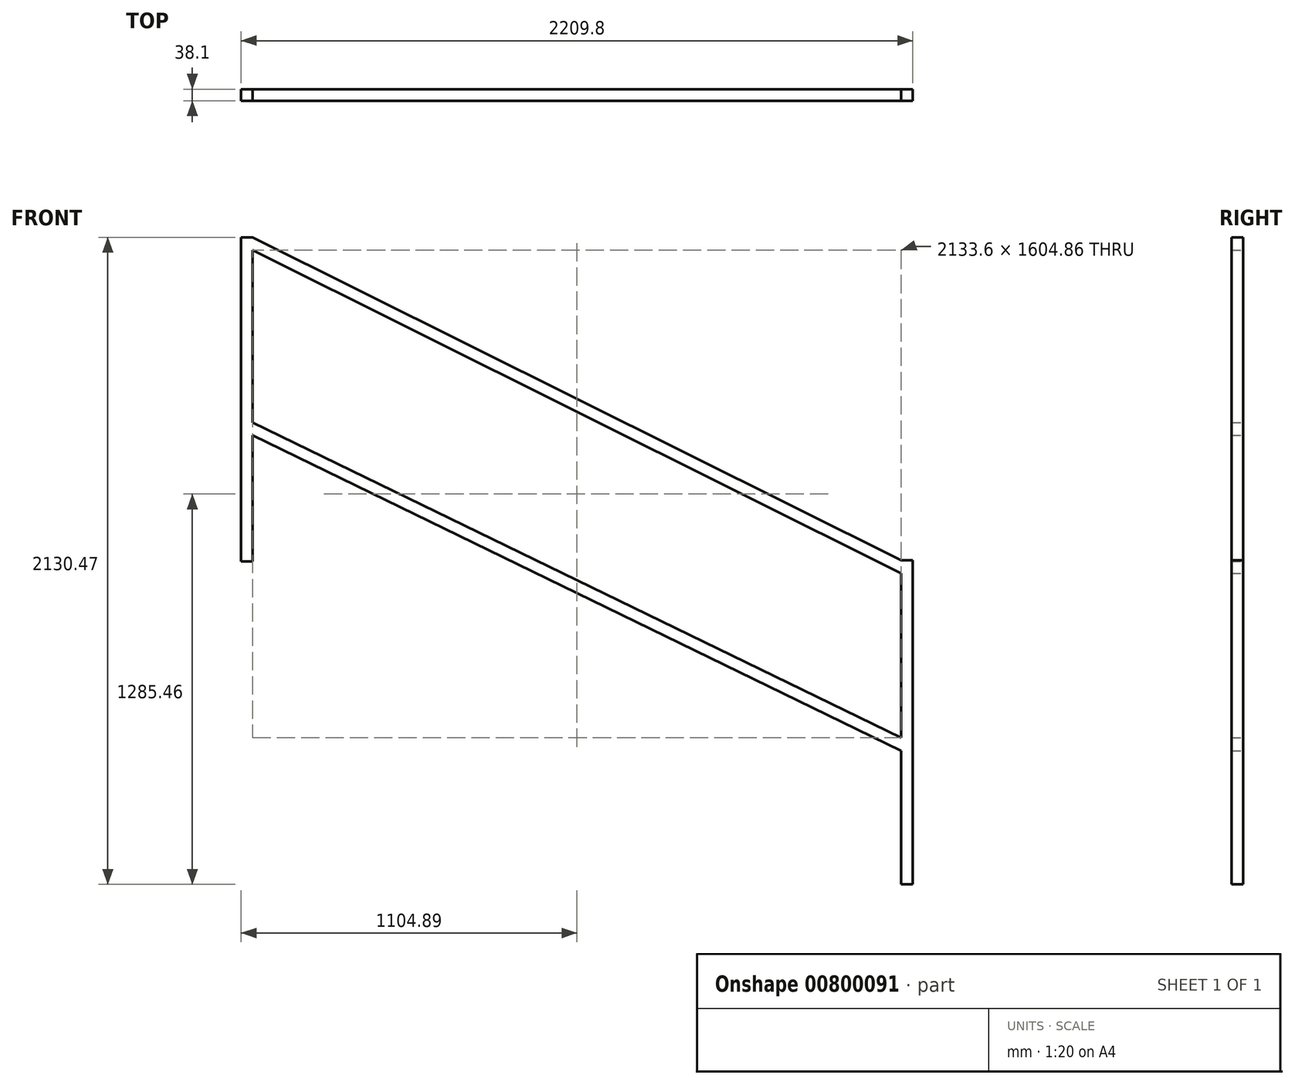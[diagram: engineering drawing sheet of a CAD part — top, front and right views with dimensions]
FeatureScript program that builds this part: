
annotation { "Feature Type Name" : "Feature", "Feature Type Description" : "" }
export const myFeature = defineFeature(function(context is Context, id is Id, definition is map)
    precondition{}
    {
        {
            var Q0;
            Q0=qCreatedBy(makeId("Front.planeOp"),FACE);
            var sketch = newSketch(context, id + "F0", { "sketchPlane" : qUnion([Q0])});
            skLineSegment(sketch, "E0.bottom", {"start": v(1096.72, 0) * mm, "end": v(1134.82, 0) * mm});
            skLineSegment(sketch, "E0.top", {"start": v(1096.72, -1066.8) * mm, "end": v(1134.82, -1066.8) * mm});
            skLineSegment(sketch, "E0.left", {"start": v(1096.72, 0) * mm, "end": v(1096.72, -1066.8) * mm});
            skLineSegment(sketch, "E0.right", {"start": v(1134.82, 0) * mm, "end": v(1134.82, -1066.8) * mm});
            skPoint(sketch, "E1", {"position": v(-1036.88, -3.13) * mm});
            skPoint(sketch, "E2", {"position": v(1096.72, 0) * mm});
            skLineSegment(sketch, "E3.bottom", {"start": v(-1036.88, -3.13) * mm, "end": v(-1074.98, -3.13) * mm});
            skLineSegment(sketch, "E3.top", {"start": v(-1036.88, 1063.67) * mm, "end": v(-1074.98, 1063.67) * mm});
            skLineSegment(sketch, "E3.left", {"start": v(-1036.88, -3.13) * mm, "end": v(-1036.88, 1063.67) * mm});
            skLineSegment(sketch, "E3.right", {"start": v(-1074.98, -3.13) * mm, "end": v(-1074.98, 1063.67) * mm});
            skLineSegment(sketch, "E4", {"start": v(-1036.88, 1063.67) * mm, "end": v(1096.72, 0) * mm});
            skPoint(sketch, "E5", {"position": v(-1036.88, 1021.1) * mm});
            skPoint(sketch, "E6", {"position": v(-1036.88, 454.07) * mm});
            skPoint(sketch, "E7", {"position": v(1096.72, -793.85) * mm});
            skPoint(sketch, "E8", {"position": v(1096.72, -42.57) * mm});
            skLineSegment(sketch, "E9", {"start": v(-1036.88, 1021.1) * mm, "end": v(1096.72, -42.57) * mm});
            skPoint(sketch, "E10", {"position": v(-1036.88, 411.5) * mm});
            skLineSegment(sketch, "E11", {"start": v(-1036.88, 454.07) * mm, "end": v(1096.72, -583.77) * mm});
            skLineSegment(sketch, "E12", {"start": v(-1036.88, 411.5) * mm, "end": v(1096.72, -626.34) * mm});
            skSolve(sketch);
        }
        {
            var Q0;
            Q0 = qSketchRegion(id + "F0", true);
            extrude(context, id + "F1", {"entities" : qUnion([Q0]), "depth" : 38.1 * mm, "offsetDistance" : 25.4 * mm});
        }
    });
